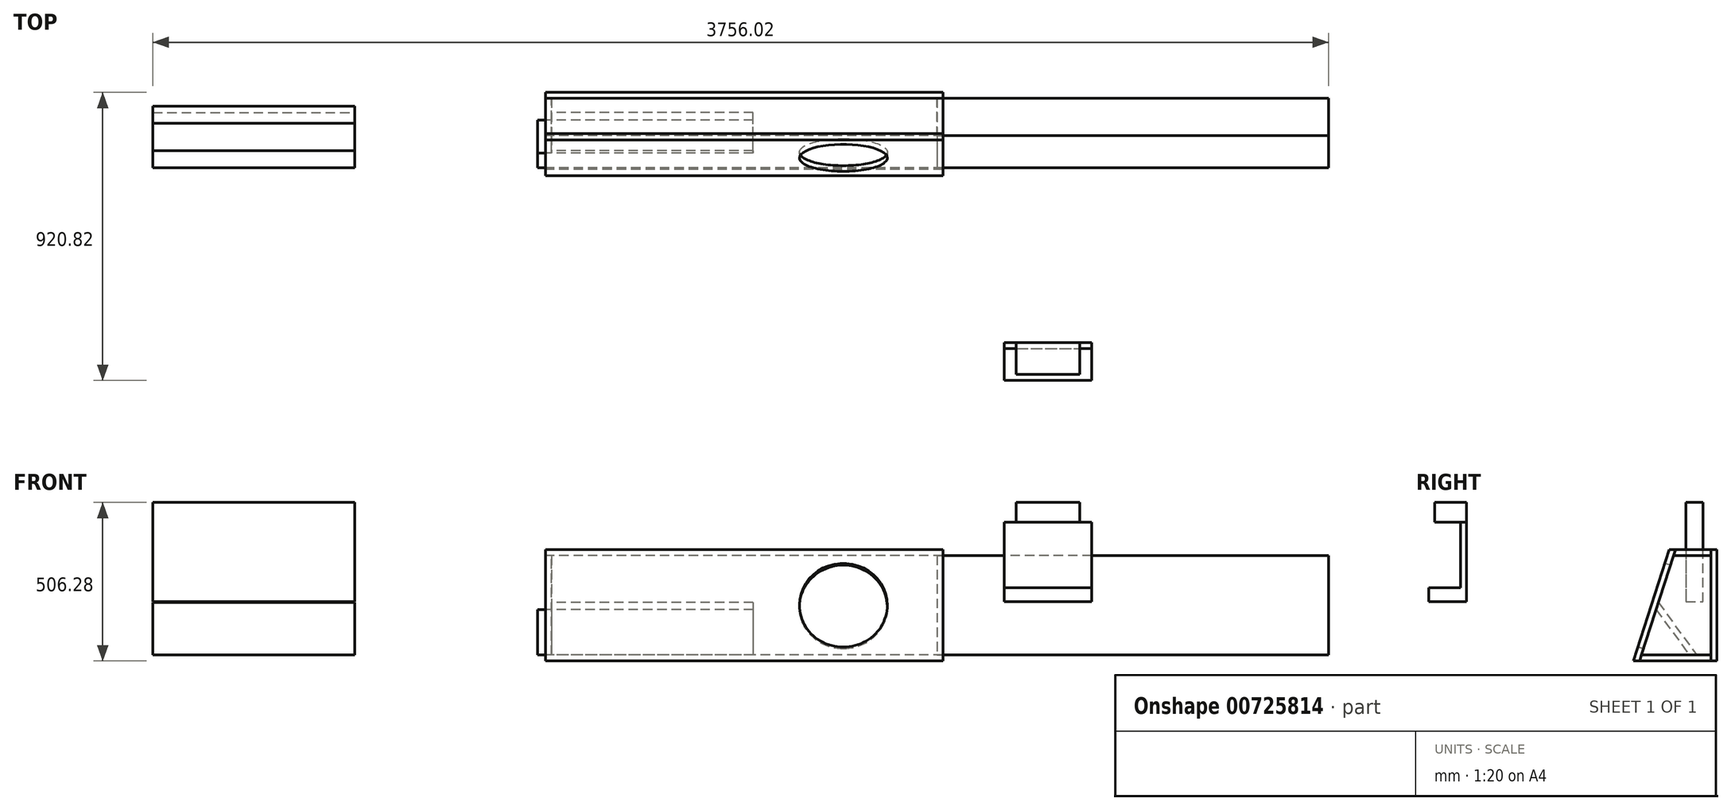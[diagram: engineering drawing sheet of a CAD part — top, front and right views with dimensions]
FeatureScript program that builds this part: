
annotation { "Feature Type Name" : "Feature", "Feature Type Description" : "" }
export const myFeature = defineFeature(function(context is Context, id is Id, definition is map)
    precondition{}
    {
        {
            var Q0;
            Q0=qCreatedBy(makeId("Right.planeOp"),FACE);
            var sketch = newSketch(context, id + "F0", { "sketchPlane" : qUnion([Q0])});
            skLineSegment(sketch, "E0", {"start": v(-168, -188.78) * mm, "end": v(98.7, -188.78) * mm});
            skLineSegment(sketch, "E1", {"start": v(98.7, -188.78) * mm, "end": v(98.7, 166.82) * mm});
            skLineSegment(sketch, "E2", {"start": v(98.7, 166.82) * mm, "end": v(-53.7, 166.82) * mm});
            skLineSegment(sketch, "E3", {"start": v(-53.7, 166.82) * mm, "end": v(-168, -188.78) * mm});
            skLineSegment(sketch, "E4.0", {"start": v(79.66, -188.78) * mm, "end": v(79.66, 166.82) * mm});
            skLineSegment(sketch, "E5.0", {"start": v(79.66, 147.77) * mm, "end": v(-39.8, 147.77) * mm});
            skLineSegment(sketch, "E6.0", {"start": v(-33.68, 166.82) * mm, "end": v(-147.98, -188.78) * mm});
            skLineSegment(sketch, "E7.trimOffspring", {"start": v(-141.86, -169.73) * mm, "end": v(79.66, -169.73) * mm});
            skLineSegment(sketch, "E8", {"start": v(-95.22, -24.64) * mm, "end": v(10.54, -169.73) * mm});
            skLineSegment(sketch, "E9.0", {"start": v(-88, -2.2) * mm, "end": v(34.12, -169.73) * mm});
            skSolve(sketch);
        }
        {
            var Q0;
            {var subQ4=sQuery(id+"F0.wireOp",EDGE,"E3");Q0=makeQuery(id+"F0.imprint","IMPRINT",FACE,{"disambiguationData":[TD([[makeQuery(id+"F0.imprint","IMPRINT",EDGE,{"derivedFrom":subQ4}),1.0]])]});}
            extrude(context, id + "F1", {"entities" : qUnion([Q0]), "depth" : 1270 * mm, "offsetDistance" : 25.4 * mm});
        }
        {
            var Q0;
            {var subQ5=sQuery(id+"F0.wireOp",EDGE,"E5.0");Q0=makeQuery(id+"F0.imprint","IMPRINT",FACE,{"disambiguationData":[TD([[makeQuery(id+"F0.imprint","IMPRINT",EDGE,{"derivedFrom":subQ5}),-1.0]])]});}
            extrude(context, id + "F2", {"entities" : qUnion([Q0]), "depth" : 1270 * mm, "offsetDistance" : 25.4 * mm});
        }
        {
            var Q0;
            {var subQ1=sQuery(id+"F0.wireOp",EDGE,"E1");Q0=makeQuery(id+"F0.imprint","IMPRINT",FACE,{"disambiguationData":[TD([[makeQuery(id+"F0.imprint","IMPRINT",EDGE,{"derivedFrom":subQ1}),1.0]])]});}
            extrude(context, id + "F3", {"entities" : qUnion([Q0]), "depth" : 1270 * mm, "offsetDistance" : 25.4 * mm});
        }
        {
            var Q0;
            {var subQ4=sQuery(id+"F0.wireOp",EDGE,"E4.0");var subQ5=sQuery(id+"F0.wireOp",EDGE,"E0");var subQ6=makeQuery(id+"F0.imprint","INTERSECT",VERTEX,{"derivedFrom":[subQ5,subQ4]});Q0=makeQuery(id+"F0.imprint","IMPRINT",FACE,{"disambiguationData":[TD([[makeQuery(id+"F0.imprint","IMPRINT",EDGE,{"disambiguationData":[TD([[subQ6,1.0]])],"derivedFrom":subQ5}),1.0]])]});}
            extrude(context, id + "F4", {"entities" : qUnion([Q0]), "depth" : 1270 * mm, "offsetDistance" : 25.4 * mm});
        }
        {
            var Q0;
            {var subQ0=sQuery(id+"F0.wireOp",EDGE,"E8");Q0=makeQuery(id+"F0.imprint","IMPRINT",FACE,{"disambiguationData":[TD([[makeQuery(id+"F0.imprint","IMPRINT",EDGE,{"derivedFrom":subQ0}),1.0]])]});}
            extrude(context, id + "F5", {"entities" : qUnion([Q0]), "depth" : 663.57 * mm, "offsetDistance" : 25.4 * mm});
        }
        {
            var Q0;
            {var subQ1=sQuery(id+"F0.wireOp",EDGE,"E5.0");Q0=makeQuery(id+"F0.imprint","IMPRINT",FACE,{"disambiguationData":[TD([[makeQuery(id+"F0.imprint","IMPRINT",EDGE,{"derivedFrom":subQ1}),1.0]])]});}
            extrude(context, id + "F6", {"entities" : qUnion([Q0]), "depth" : 19.05 * mm, "offsetDistance" : 25.4 * mm});
        }
        {
            var Q0;
            Q0=makeQuery(id+"F6.opExtrude","SWEPT_BODY",BODY,{"disambiguationData":[OSD([sQuery(id+"F0.wireOp",EDGE,"E4.0"),sQuery(id+"F0.wireOp",EDGE,"E5.0"),sQuery(id+"F0.wireOp",EDGE,"E6.0"),sQuery(id+"F0.wireOp",EDGE,"E7.trimOffspring"),sQuery(id+"F0.wireOp",EDGE,"E9.0")])]});
            deleteBodies(context, id + "F7", {"entities" : qUnion([Q0])});
        }
        {
            var Q0;
            {var subQ0=sQuery(id+"F0.wireOp",EDGE,"E8");Q0=makeQuery(id+"F0.imprint","IMPRINT",FACE,{"disambiguationData":[TD([[makeQuery(id+"F0.imprint","IMPRINT",EDGE,{"derivedFrom":subQ0}),1.0]])]});}
            extrude(context, id + "F8", {"entities" : qUnion([Q0]), "operationType" : NewBodyOperationType.REMOVE, "depth" : 19.05 * mm, "offsetDistance" : 25.4 * mm});
        }
        {
            var Q0;
            {var subQ1=sQuery(id+"F0.wireOp",EDGE,"E1");Q0=makeQuery(id+"F0.imprint","IMPRINT",FACE,{"disambiguationData":[TD([[makeQuery(id+"F0.imprint","IMPRINT",EDGE,{"derivedFrom":subQ1}),1.0]])]});}
            var sketch = newSketch(context, id + "F9", { "sketchPlane" : qUnion([Q0])});
            skPoint(sketch, "E10.0", {"position": v(79.66, 147.77) * mm});
            skPoint(sketch, "E11.0", {"position": v(-39.8, 147.77) * mm});
            skPoint(sketch, "E12.0", {"position": v(10.54, -169.73) * mm});
            skPoint(sketch, "E13.0", {"position": v(79.66, -169.73) * mm});
            skLineSegment(sketch, "E14", {"start": v(79.66, 147.77) * mm, "end": v(-39.8, 147.77) * mm});
            skPoint(sketch, "E15.0", {"position": v(-95.22, -24.64) * mm});
            skLineSegment(sketch, "E16", {"start": v(-39.8, 147.77) * mm, "end": v(-95.22, -24.64) * mm});
            skLineSegment(sketch, "E17", {"start": v(-95.22, -24.64) * mm, "end": v(10.54, -169.73) * mm});
            skLineSegment(sketch, "E18", {"start": v(10.54, -169.73) * mm, "end": v(79.66, -169.73) * mm});
            skLineSegment(sketch, "E19", {"start": v(79.66, -169.73) * mm, "end": v(79.66, 147.77) * mm});
            skSolve(sketch);
        }
        {
            var Q0;
            Q0 = qSketchRegion(id + "F9", true);
            extrude(context, id + "F10", {"entities" : qUnion([Q0]), "depth" : 19.05 * mm, "offsetDistance" : 25.4 * mm});
        }
        {
            var Q0;
            Q0=makeQuery(id+"F1.opExtrude","CAP_FACE",FACE,{"disambiguationData":[OSD([sQuery(id+"F0.wireOp",EDGE,"E0"),sQuery(id+"F0.wireOp",EDGE,"E2"),sQuery(id+"F0.wireOp",EDGE,"E3"),sQuery(id+"F0.wireOp",EDGE,"E6.0")])],"isStart":false});
            var sketch = newSketch(context, id + "F11", { "sketchPlane" : qUnion([Q0])});
            skPoint(sketch, "E20.0", {"position": v(-39.8, 147.77) * mm});
            skPoint(sketch, "E21.0", {"position": v(79.66, 147.77) * mm});
            skPoint(sketch, "E22.0", {"position": v(79.66, -169.73) * mm});
            skPoint(sketch, "E23.0", {"position": v(-141.86, -169.73) * mm});
            skLineSegment(sketch, "E24", {"start": v(-39.8, 147.77) * mm, "end": v(79.66, 147.77) * mm});
            skLineSegment(sketch, "E25", {"start": v(79.66, 147.77) * mm, "end": v(79.66, -169.73) * mm});
            skLineSegment(sketch, "E26", {"start": v(79.66, -169.73) * mm, "end": v(-141.86, -169.73) * mm});
            skLineSegment(sketch, "E27", {"start": v(-141.86, -169.73) * mm, "end": v(-39.8, 147.77) * mm});
            skSolve(sketch);
        }
        {
            var Q0;
            Q0 = qSketchRegion(id + "F11", true);
            extrude(context, id + "F12", {"entities" : qUnion([Q0]), "oppositeDirection" : true, "depth" : 19.05 * mm, "offsetDistance" : 25.4 * mm});
        }
        {
            var Q0;
            Q0=makeQuery(id+"F12.opExtrude","CAP_FACE",FACE,{"disambiguationData":[OSD([sQuery(id+"F11.wireOp",EDGE,"E24"),sQuery(id+"F11.wireOp",EDGE,"E25"),sQuery(id+"F11.wireOp",EDGE,"E26"),sQuery(id+"F11.wireOp",EDGE,"E27")])],"isStart":true});
            var sketch = newSketch(context, id + "F13", { "sketchPlane" : qUnion([Q0])});
            skLineSegment(sketch, "E28", {"start": v(-39.8, 147.77) * mm, "end": v(79.66, 147.77) * mm});
            skLineSegment(sketch, "E29", {"start": v(79.66, 147.77) * mm, "end": v(79.66, -169.73) * mm});
            skLineSegment(sketch, "E30", {"start": v(79.66, -169.73) * mm, "end": v(-141.86, -169.73) * mm});
            skLineSegment(sketch, "E31", {"start": v(-141.86, -169.73) * mm, "end": v(-39.8, 147.77) * mm});
            skSolve(sketch);
        }
        {
            var Q0;
            Q0 = qSketchRegion(id + "F13", true);
            extrude(context, id + "F14", {"entities" : qUnion([Q0]), "depth" : 1231.9 * mm, "offsetDistance" : 25.4 * mm});
        }
        {
            var Q0;
            {var subQ0=sQuery(id+"F0.wireOp",EDGE,"E8");Q0=makeQuery(id+"F0.imprint","IMPRINT",FACE,{"disambiguationData":[TD([[makeQuery(id+"F0.imprint","IMPRINT",EDGE,{"derivedFrom":subQ0}),1.0]])]});}
            cPlane(context, id + "F15", {"entities" : qUnion([Q0]), "cplaneType" : CPlaneType.OFFSET, "offset" : 609.6 * mm, "oppositeDirection" : true, "width" : 152.4 * mm, "height" : 152.4 * mm});
        }
        {
            var Q0;
            Q0=qCreatedBy(id+"F15.planeOp",FACE);
            var sketch = newSketch(context, id + "F16", { "sketchPlane" : qUnion([Q0])});
            skPoint(sketch, "E32.0", {"position": v(-88, -2.2) * mm});
            skPoint(sketch, "E33.0", {"position": v(34.12, -169.73) * mm});
            skPoint(sketch, "E34.0", {"position": v(-141.86, -169.73) * mm});
            skLineSegment(sketch, "E35", {"start": v(-88, -2.2) * mm, "end": v(34.12, -169.73) * mm});
            skLineSegment(sketch, "E36", {"start": v(-141.86, -169.73) * mm, "end": v(-88, -2.2) * mm});
            skLineSegment(sketch, "E37", {"start": v(34.12, -169.73) * mm, "end": v(-141.86, -169.73) * mm});
            skSolve(sketch);
        }
        {
            var Q0;
            Q0 = qSketchRegion(id + "F16", true);
            extrude(context, id + "F17", {"entities" : qUnion([Q0]), "oppositeDirection" : true, "depth" : 644.52 * mm, "offsetDistance" : 25.4 * mm});
        }
        {
            var Q0;
            Q0=qCreatedBy(id+"F15.planeOp",FACE);
            var sketch = newSketch(context, id + "F18", { "sketchPlane" : qUnion([Q0])});
            skLineSegment(sketch, "E38", {"start": v(0, 0) * mm, "end": v(53.98, 0) * mm});
            skLineSegment(sketch, "E39", {"start": v(53.98, 0) * mm, "end": v(53.98, 317.5) * mm});
            skLineSegment(sketch, "E40", {"start": v(53.98, 317.5) * mm, "end": v(0, 317.5) * mm});
            skLineSegment(sketch, "E41", {"start": v(0, 317.5) * mm, "end": v(0, 0) * mm});
            skSolve(sketch);
        }
        {
            var Q0;
            Q0 = qSketchRegion(id + "F18", true);
            extrude(context, id + "F19", {"entities" : qUnion([Q0]), "oppositeDirection" : true, "depth" : 644.52 * mm, "offsetDistance" : 25.4 * mm});
        }
        {
            var Q0;
            {var subQ4=sQuery(id+"F0.wireOp",EDGE,"E3");Q0=makeQuery(id+"F0.imprint","IMPRINT",FACE,{"disambiguationData":[TD([[makeQuery(id+"F0.imprint","IMPRINT",EDGE,{"derivedFrom":subQ4}),1.0]])]});}
            var sketch = newSketch(context, id + "F20", { "sketchPlane" : qUnion([Q0])});
            skPoint(sketch, "E42.0", {"position": v(-95.22, -24.64) * mm});
            skPoint(sketch, "E43.0", {"position": v(10.54, -169.73) * mm});
            skPoint(sketch, "E44.0", {"position": v(-141.86, -169.73) * mm});
            skLineSegment(sketch, "E45", {"start": v(-95.22, -24.64) * mm, "end": v(10.54, -169.73) * mm});
            skLineSegment(sketch, "E46", {"start": v(-141.86, -169.73) * mm, "end": v(-95.22, -24.64) * mm});
            skSolve(sketch);
        }
        {
            var Q0;
            {var subQ3=sQuery(id+"F0.wireOp",EDGE,"E8");Q0=makeQuery(id+"F0.imprint","IMPRINT",FACE,{"disambiguationData":[TD([[makeQuery(id+"F0.imprint","IMPRINT",EDGE,{"derivedFrom":subQ3}),-1.0]])]});}
            extrude(context, id + "F21", {"entities" : qUnion([Q0]), "oppositeDirection" : true, "depth" : 25.4 * mm, "offsetDistance" : 25.4 * mm});
        }
        {
            var Q0;
            Q0=makeQuery(id+"F1.opExtrude","SWEPT_FACE",FACE,{"disambiguationData":[OSD([sQuery(id+"F0.wireOp",EDGE,"E3")])]});
            var sketch = newSketch(context, id + "F22", { "sketchPlane" : qUnion([Q0])});
            skLineSegment(sketch, "E47", {"start": v(1270, -44.37) * mm, "end": v(951.83, -44.37) * mm, "construction": true});
            skCircle(sketch, "E48", {"center": v(951.83, -44.37) * mm, "radius": 140.5 * mm});
            skSolve(sketch);
        }
        {
            var Q0;
            Q0 = qSketchRegion(id + "F22", true);
            extrude(context, id + "F23", {"entities" : qUnion([Q0]), "operationType" : NewBodyOperationType.REMOVE, "oppositeDirection" : true, "depth" : 25.4 * mm, "offsetDistance" : 25.4 * mm});
        }
        {
            var Q0;
            Q0=makeQuery(id+"F21.opExtrude","SWEPT_BODY",BODY,{"disambiguationData":[OSD([sQuery(id+"F0.wireOp",EDGE,"E6.0"),sQuery(id+"F0.wireOp",EDGE,"E7.trimOffspring"),sQuery(id+"F0.wireOp",EDGE,"E8")])]});
            deleteBodies(context, id + "F24", {"entities" : qUnion([Q0])});
        }
        {
            var Q0;
            Q0=qCreatedBy(makeId("Top.planeOp"),FACE);
            var sketch = newSketch(context, id + "F25", { "sketchPlane" : qUnion([Q0])});
            skLineSegment(sketch, "E49", {"start": v(1466.46, -701.46) * mm, "end": v(1745.86, -701.46) * mm});
            skLineSegment(sketch, "E50", {"start": v(1745.86, -701.46) * mm, "end": v(1745.86, -822.1) * mm});
            skLineSegment(sketch, "E51", {"start": v(1745.86, -822.1) * mm, "end": v(1466.46, -822.1) * mm});
            skLineSegment(sketch, "E52", {"start": v(1466.46, -822.1) * mm, "end": v(1466.46, -701.46) * mm});
            skSolve(sketch);
        }
        {
            var Q0;
            Q0=makeQuery(id+"F25.imprint","IMPRINT",FACE,{"disambiguationData":[TD([[makeQuery(id+"F25.imprint","IMPRINT",EDGE,{"derivedFrom":sQuery(id+"F25.wireOp",EDGE,"E49")}),-1.0]])]});
            extrude(context, id + "F26", {"entities" : qUnion([Q0]), "depth" : 44.45 * mm, "offsetDistance" : 25.4 * mm});
        }
        {
            var Q0;
            Q0=makeQuery(id+"F26.opExtrude","CAP_FACE",FACE,{"disambiguationData":[OSD([sQuery(id+"F25.wireOp",EDGE,"E49"),sQuery(id+"F25.wireOp",EDGE,"E50"),sQuery(id+"F25.wireOp",EDGE,"E51"),sQuery(id+"F25.wireOp",EDGE,"E52")])],"isStart":false});
            var sketch = newSketch(context, id + "F27", { "sketchPlane" : qUnion([Q0])});
            skLineSegment(sketch, "E53", {"start": v(1466.46, -701.46) * mm, "end": v(1466.46, -720.5) * mm});
            skLineSegment(sketch, "E54", {"start": v(1466.46, -720.5) * mm, "end": v(1745.86, -720.5) * mm});
            skLineSegment(sketch, "E55", {"start": v(1745.86, -720.5) * mm, "end": v(1745.86, -701.46) * mm});
            skLineSegment(sketch, "E56", {"start": v(1745.86, -701.46) * mm, "end": v(1466.46, -701.46) * mm});
            skSolve(sketch);
        }
        {
            var Q0;
            Q0 = qSketchRegion(id + "F27", true);
            extrude(context, id + "F28", {"entities" : qUnion([Q0]), "operationType" : NewBodyOperationType.ADD, "depth" : 209.55 * mm, "offsetDistance" : 25.4 * mm});
        }
        {
            var Q0;
            Q0=makeQuery(id+"F28.opExtrude","CAP_FACE",FACE,{"disambiguationData":[OSD([sQuery(id+"F27.wireOp",EDGE,"E53"),sQuery(id+"F27.wireOp",EDGE,"E54"),sQuery(id+"F27.wireOp",EDGE,"E55"),sQuery(id+"F27.wireOp",EDGE,"E56")])],"isStart":false});
            var sketch = newSketch(context, id + "F29", { "sketchPlane" : qUnion([Q0])});
            skLineSegment(sketch, "E57", {"start": v(1606.16, -720.5) * mm, "end": v(1707.76, -720.5) * mm});
            skLineSegment(sketch, "E58", {"start": v(1707.76, -720.5) * mm, "end": v(1707.76, -701.46) * mm});
            skLineSegment(sketch, "E59", {"start": v(1707.76, -701.46) * mm, "end": v(1504.56, -701.46) * mm});
            skLineSegment(sketch, "E60", {"start": v(1504.56, -701.46) * mm, "end": v(1504.56, -720.5) * mm});
            skLineSegment(sketch, "E61", {"start": v(1504.56, -720.5) * mm, "end": v(1606.16, -720.5) * mm});
            skSolve(sketch);
        }
        {
            var Q0;
            Q0 = qSketchRegion(id + "F29", true);
            extrude(context, id + "F30", {"entities" : qUnion([Q0]), "operationType" : NewBodyOperationType.ADD, "depth" : 63.5 * mm, "offsetDistance" : 25.4 * mm});
        }
        {
            var Q0;
            Q0=makeQuery(id+"F30.boolean.opBoolean","MERGE",FACE,{"derivedFrom":[makeQuery(id+"F28.opExtrude","SWEPT_FACE",FACE,{"disambiguationData":[OSD([sQuery(id+"F27.wireOp",EDGE,"E54")])]}),makeQuery(id+"F30.opExtrude","SWEPT_FACE",FACE,{"disambiguationData":[OSD([sQuery(id+"F29.wireOp",EDGE,"E57"),sQuery(id+"F29.wireOp",EDGE,"E61")])]})]});
            var sketch = newSketch(context, id + "F31", { "sketchPlane" : qUnion([Q0])});
            skLineSegment(sketch, "E62", {"start": v(1504.56, 317.5) * mm, "end": v(1504.56, 254) * mm});
            skLineSegment(sketch, "E63", {"start": v(1504.56, 254) * mm, "end": v(1707.76, 254) * mm});
            skLineSegment(sketch, "E64", {"start": v(1707.76, 254) * mm, "end": v(1707.76, 317.5) * mm});
            skLineSegment(sketch, "E65", {"start": v(1707.76, 317.5) * mm, "end": v(1504.56, 317.5) * mm});
            skSolve(sketch);
        }
        {
            var Q0;
            Q0=makeQuery(id+"F31.imprint","IMPRINT",FACE,{"disambiguationData":[TD([[makeQuery(id+"F31.imprint","IMPRINT",EDGE,{"derivedFrom":sQuery(id+"F31.wireOp",EDGE,"E62")}),1.0]])]});
            extrude(context, id + "F32", {"entities" : qUnion([Q0]), "operationType" : NewBodyOperationType.ADD, "depth" : 82.55 * mm, "offsetDistance" : 25.4 * mm});
        }
        {
            var Q0;
            Q0=makeQuery(id+"F20.imprint","IMPRINT",FACE,{"disambiguationData":[TD([[makeQuery(id+"F20.imprint","IMPRINT",EDGE,{"derivedFrom":sQuery(id+"F20.wireOp",EDGE,"E46")}),-1.0]])]});
            var sketch = newSketch(context, id + "F33", { "sketchPlane" : qUnion([Q0])});
            skPoint(sketch, "E66.0", {"position": v(-95.22, -24.64) * mm});
            skPoint(sketch, "E67.0", {"position": v(10.54, -169.73) * mm});
            skPoint(sketch, "E68.0", {"position": v(-141.86, -169.73) * mm});
            skLineSegment(sketch, "E69", {"start": v(-95.22, -24.64) * mm, "end": v(10.54, -169.73) * mm});
            skLineSegment(sketch, "E70", {"start": v(-141.86, -169.73) * mm, "end": v(-95.22, -24.64) * mm});
            skLineSegment(sketch, "E71", {"start": v(-141.86, -169.73) * mm, "end": v(10.54, -169.73) * mm});
            skSolve(sketch);
        }
        {
            var Q0;
            Q0 = qSketchRegion(id + "F33", true);
            extrude(context, id + "F34", {"entities" : qUnion([Q0]), "oppositeDirection" : true, "depth" : 25.4 * mm, "offsetDistance" : 25.4 * mm});
        }
    });
